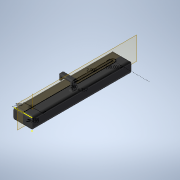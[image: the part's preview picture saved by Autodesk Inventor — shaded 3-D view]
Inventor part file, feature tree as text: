
AUTODESK INVENTOR PART (.ipt)
format: ipt  version: 2020 (Build 240168000, 168)  size: 235,008 bytes
history: native  units: in
note: dims shown in document units (in); Inventor stores cm internally (conversion verified against a paired STEP export)
features: sketch x6, extrude x5, hole x2, fillet x2, plane x1, other x1, revolve x1
ambient origin geometry x8: Origin, YZ Plane, XZ Plane, XY Plane, X Axis, Y Axis, Z Axis, Center Point
bodies: Solid1 (feature_tree)
feature tree (18):
  extrude  "Extrusion1"  Depth=5.357in
  sketch  "Sketch2"  dims[d2=0.625in d3=0.0in d4=0.5in d5=4.357in]
  hole  "Hole1"  [1 undecoded]
  fillet  "Fillet1"  Radius=4.357in
  extrude  "Extrusion2"  Depth=0.125in
  extrude  "Extrusion3"  TaperAngle=0.0deg  [1 undecoded]
  fillet  "Fillet2"  Radius=0.125in
  hole  "Hole2"  [1 undecoded]
  extrude  "Extrusion4"  TaperAngle=135.0deg  [1 undecoded]
  sketch  "Sketch6"  dims[d17=0.25in d18=0.5in d19=0.0in]
  extrude  "Extrusion5"  Depth=0.5in TaperAngle=0.0deg
  plane  "Work Plane1"
  other  "Work Axis2"
  revolve  "Revolution1"  [1 undecoded]
  sketch  "Sketch1"  dims[d0=1.0in d1=5.357in]
  sketch  "Sketch3"  dims[d6=0.266in d7=0.5in d8=0.438in d9=0.25in d10=0.5635in d11=0.75in d12=0.8108in d13=0.125in]
  sketch  "Sketch4"  dims[d14=2.3035in d15=0.0in d16=0.125in]
  sketch  "Sketch8"  dims[d20=0.2in d21=135.0deg d22=0.5in d23=0.0in d24=0.0625in d25=0.332in d26=0.75in d27=0.531in d28=0.313in d29=0.5635in d30=1.0in d31=0.8108in d32=2.0in d33=90.0deg d34=0.26in d35=0.5in d36=0.0in d39=0.43in d40=0.5in d41=0.5in d42=0.0in d48=0.2894in d49=0.0in d50=0.0687in]
note: 5 required parameter values undecoded (feature->parameter linkage not recoverable at this tier; creation-order binding heuristic only, values carry confidence <= 0.55)